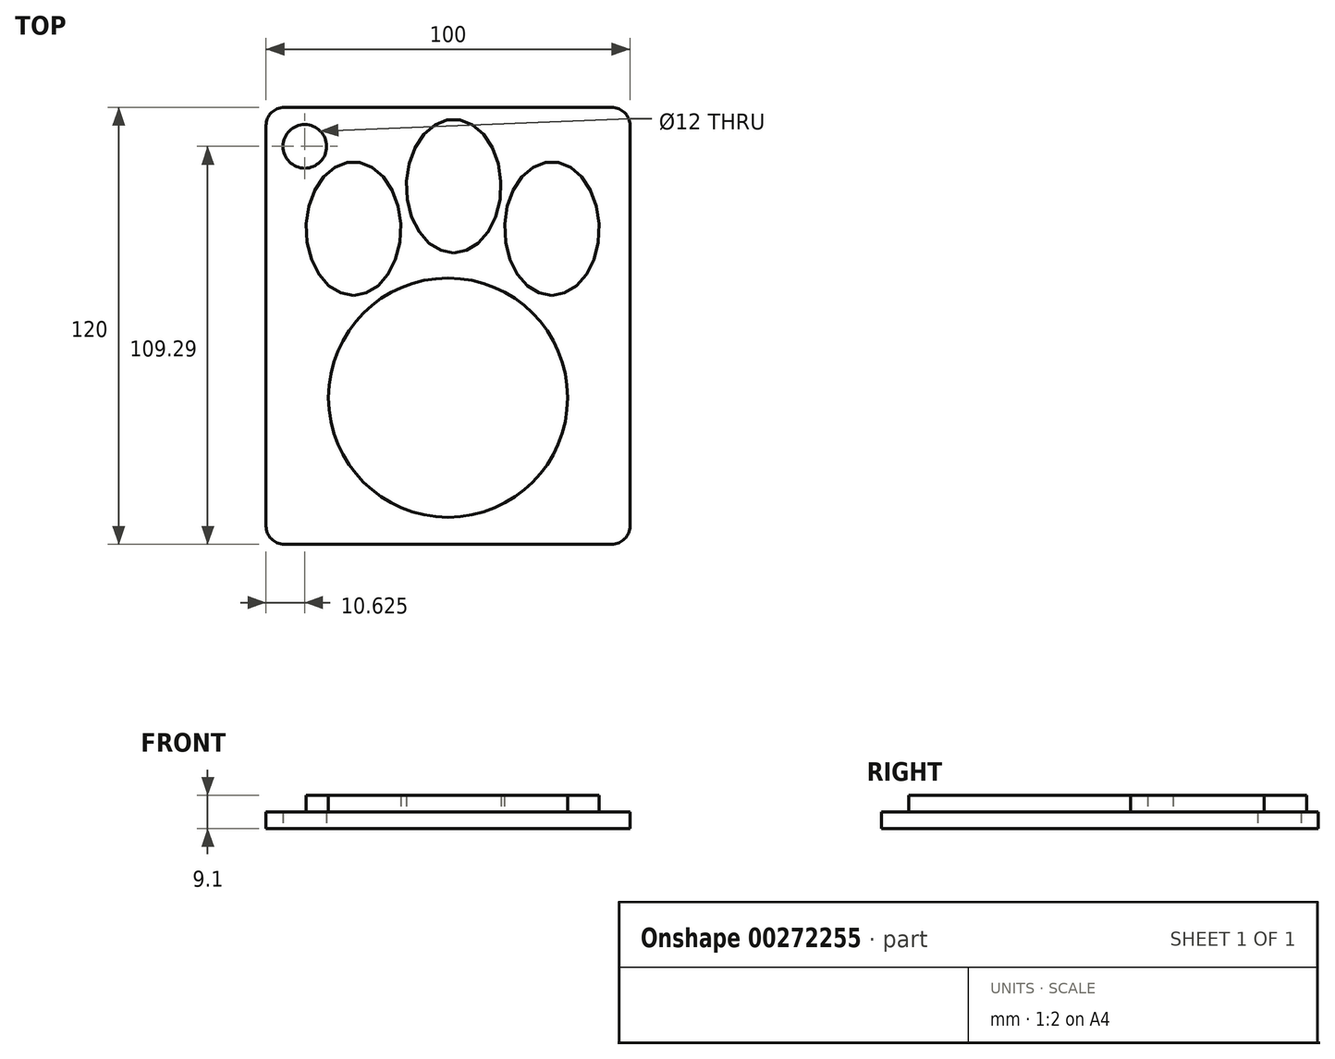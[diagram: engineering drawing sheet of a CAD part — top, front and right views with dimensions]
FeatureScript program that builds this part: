
annotation { "Feature Type Name" : "Feature", "Feature Type Description" : "" }
export const myFeature = defineFeature(function(context is Context, id is Id, definition is map)
    precondition{}
    {
        {
            var Q0;
            Q0=qCreatedBy(makeId("Top.planeOp"),FACE);
            var sketch = newSketch(context, id + "F0", { "sketchPlane" : qUnion([Q0])});
            skLineSegment(sketch, "E0.bottom", {"start": v(-50, 60) * mm, "end": v(50, 60) * mm});
            skLineSegment(sketch, "E0.top", {"start": v(-50, -60) * mm, "end": v(50, -60) * mm});
            skLineSegment(sketch, "E0.left", {"start": v(-50, 60) * mm, "end": v(-50, -60) * mm});
            skLineSegment(sketch, "E0.right", {"start": v(50, 60) * mm, "end": v(50, -60) * mm});
            skPoint(sketch, "E0.middle", {"position": v(0, 0) * mm});
            skCircle(sketch, "E1", {"center": v(-39.38, 49.29) * mm, "radius": 6 * mm});
            skSolve(sketch);
        }
        {
            var Q0;
            Q0=makeQuery(id+"F0.imprint","IMPRINT",FACE,{"disambiguationData":[TD([[makeQuery(id+"F0.imprint","IMPRINT",EDGE,{"derivedFrom":sQuery(id+"F0.wireOp",EDGE,"E0.bottom")}),-1.0]])]});
            extrude(context, id + "F1", {"entities" : qUnion([Q0]), "depth" : 4.5 * mm});
        }
        {
            var Q0;
            Q0=makeQuery(id+"F1.opExtrude","SWEPT_EDGE",EDGE,{"disambiguationData":[OSD([sQuery(id+"F0.wireOp",EDGE,"E0.top"),sQuery(id+"F0.wireOp",EDGE,"E0.left")])]});
            var Q1;
            Q1=makeQuery(id+"F1.opExtrude","SWEPT_EDGE",EDGE,{"disambiguationData":[OSD([sQuery(id+"F0.wireOp",EDGE,"E0.top"),sQuery(id+"F0.wireOp",EDGE,"E0.right")])]});
            var Q2;
            Q2=makeQuery(id+"F1.opExtrude","SWEPT_EDGE",EDGE,{"disambiguationData":[OSD([sQuery(id+"F0.wireOp",EDGE,"E0.bottom"),sQuery(id+"F0.wireOp",EDGE,"E0.right")])]});
            var Q3;
            Q3=makeQuery(id+"F1.opExtrude","SWEPT_EDGE",EDGE,{"disambiguationData":[OSD([sQuery(id+"F0.wireOp",EDGE,"E0.bottom"),sQuery(id+"F0.wireOp",EDGE,"E0.left")])]});
            fillet(context, id + "F2", {"entities" : qUnion([Q0, Q1, Q2, Q3]), "radius" : 5 * mm, "tangentPropagation" : true, "allowEdgeOverflow" : false});
        }
        {
            var Q0;
            Q0=makeQuery(id+"F1.opExtrude","CAP_FACE",FACE,{"disambiguationData":[OSD([sQuery(id+"F0.wireOp",EDGE,"E0.bottom"),sQuery(id+"F0.wireOp",EDGE,"E0.top"),sQuery(id+"F0.wireOp",EDGE,"E0.left"),sQuery(id+"F0.wireOp",EDGE,"E0.right"),sQuery(id+"F0.wireOp",EDGE,"E1")])],"isStart":false});
            var sketch = newSketch(context, id + "F3", { "sketchPlane" : qUnion([Q0])});
            skEllipse(sketch, "E2", {"center": v(-25.99, 26.7) * mm, "majorRadius": 18.35 * mm, "minorRadius": 13 * mm, "majorAxis": v(0, -1)});
            skEllipse(sketch, "E3", {"center": v(1.55, 38.4) * mm, "majorRadius": 18.35 * mm, "minorRadius": 13 * mm, "majorAxis": v(0, -1)});
            skEllipse(sketch, "E4", {"center": v(28.53, 26.7) * mm, "majorRadius": 18.35 * mm, "minorRadius": 13 * mm, "majorAxis": v(0, -1)});
            skCircle(sketch, "E5", {"center": v(0, -19.75) * mm, "radius": 32.85 * mm});
            skPoint(sketch, "E5.first.point", {"position": v(-10, 11.54) * mm});
            skPoint(sketch, "E5.second.point", {"position": v(14.33, -49.3) * mm});
            skPoint(sketch, "E5.third.point", {"position": v(13.58, -49.66) * mm});
            skSolve(sketch);
        }
        {
            var Q0;
            Q0=makeQuery(id+"F3.imprint","IMPRINT",FACE,{"disambiguationData":[TD([[makeQuery(id+"F3.imprint","IMPRINT",EDGE,{"derivedFrom":sQuery(id+"F3.wireOp",EDGE,"E5")}),1.0]])]});
            var Q1;
            Q1=makeQuery(id+"F3.imprint","IMPRINT",FACE,{"disambiguationData":[TD([[makeQuery(id+"F3.imprint","IMPRINT",EDGE,{"derivedFrom":sQuery(id+"F3.wireOp",EDGE,"E2")}),1.0]])]});
            var Q2;
            Q2=makeQuery(id+"F3.imprint","IMPRINT",FACE,{"disambiguationData":[TD([[makeQuery(id+"F3.imprint","IMPRINT",EDGE,{"derivedFrom":sQuery(id+"F3.wireOp",EDGE,"E3")}),1.0]])]});
            var Q3;
            Q3=makeQuery(id+"F3.imprint","IMPRINT",FACE,{"disambiguationData":[TD([[makeQuery(id+"F3.imprint","IMPRINT",EDGE,{"derivedFrom":sQuery(id+"F3.wireOp",EDGE,"E4")}),1.0]])]});
            extrude(context, id + "F4", {"entities" : qUnion([Q0, Q1, Q2, Q3]), "operationType" : NewBodyOperationType.ADD, "depth" : 4.6 * mm});
        }
    });
